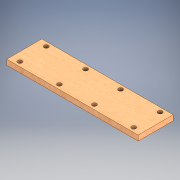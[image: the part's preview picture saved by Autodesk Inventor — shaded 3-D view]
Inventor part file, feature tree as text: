
AUTODESK INVENTOR PART (.ipt)
format: ipt  version: 2020 (Build 240168000, 168)  size: 141,312 bytes
history: native  units: mm
features: extrude x1, sketch x1
ambient origin geometry x8: Origin, YZ Plane, XZ Plane, XY Plane, X Axis, Y Axis, Z Axis, Center Point
bodies: Solide1 (feature_tree)
feature tree (2):
  extrude  "Extrusion1"  Depth=150.0mm
  sketch  "Esquisse1"
